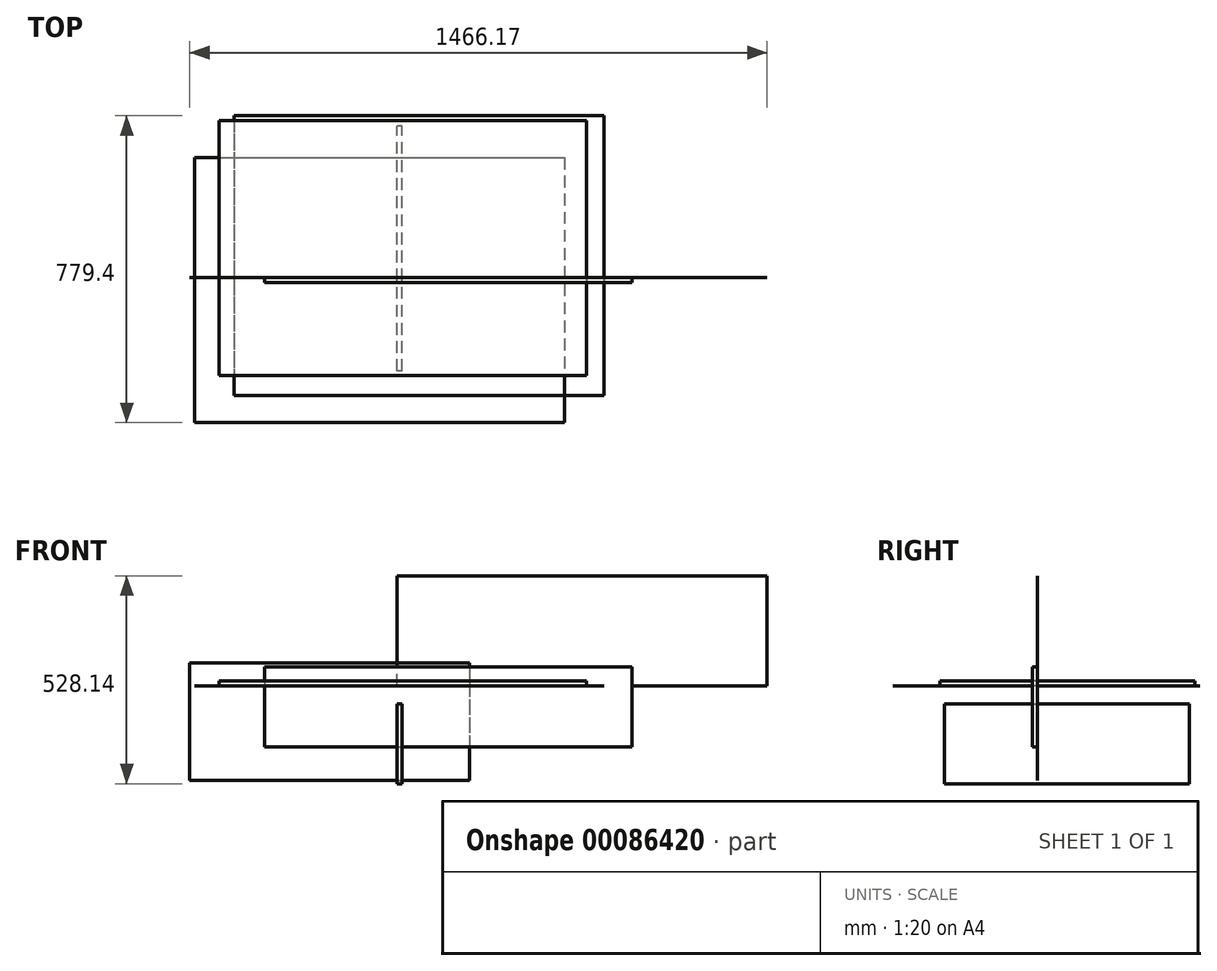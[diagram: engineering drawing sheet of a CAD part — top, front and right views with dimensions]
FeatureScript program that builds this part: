
annotation { "Feature Type Name" : "Feature", "Feature Type Description" : "" }
export const myFeature = defineFeature(function(context is Context, id is Id, definition is map)
    precondition{}
    {
        {
            var Q0;
            Q0=qCreatedBy(makeId("Front.planeOp"),FACE);
            var sketch = newSketch(context, id + "F0", { "sketchPlane" : qUnion([Q0])});
            skLineSegment(sketch, "E0.bottom", {"start": v(0, 0) * mm, "end": v(939.8, 0) * mm});
            skLineSegment(sketch, "E0.top", {"start": v(0, 279.4) * mm, "end": v(939.8, 279.4) * mm});
            skLineSegment(sketch, "E0.left", {"start": v(0, 0) * mm, "end": v(0, 279.4) * mm});
            skLineSegment(sketch, "E0.right", {"start": v(939.8, 0) * mm, "end": v(939.8, 279.4) * mm});
            skSolve(sketch);
        }
        {
            var Q0;
            Q0=makeQuery(id+"F0.imprint","IMPRINT",FACE,{"disambiguationData":[TD([[makeQuery(id+"F0.imprint","IMPRINT",EDGE,{"derivedFrom":sQuery(id+"F0.wireOp",EDGE,"E0.bottom")}),1.0]])]});
            extrude(context, id + "F1", {"entities" : qUnion([Q0]), "depth" : 3 / 101.6 * mm});
        }
        {
            var Q0;
            Q0=qCreatedBy(makeId("Top.planeOp"),FACE);
            var sketch = newSketch(context, id + "F2", { "sketchPlane" : qUnion([Q0])});
            skLineSegment(sketch, "E1.bottom", {"start": v(-413.3, 411.7) * mm, "end": v(526.5, 411.7) * mm});
            skLineSegment(sketch, "E1.top", {"start": v(-413.3, -299.5) * mm, "end": v(526.5, -299.5) * mm});
            skLineSegment(sketch, "E1.left", {"start": v(-413.3, 411.7) * mm, "end": v(-413.3, -299.5) * mm});
            skLineSegment(sketch, "E1.right", {"start": v(526.5, 411.7) * mm, "end": v(526.5, -299.5) * mm});
            skSolve(sketch);
        }
        {
            var Q0;
            Q0=makeQuery(id+"F2.imprint","IMPRINT",FACE,{"disambiguationData":[TD([[makeQuery(id+"F2.imprint","IMPRINT",EDGE,{"derivedFrom":sQuery(id+"F2.wireOp",EDGE,"E1.bottom")}),-1.0]])]});
            extrude(context, id + "F3", {"entities" : qUnion([Q0]), "depth" : 3 / 101.6 * mm});
        }
        {
            var Q0;
            Q0=qCreatedBy(makeId("Top.planeOp"),FACE);
            var sketch = newSketch(context, id + "F4", { "sketchPlane" : qUnion([Q0])});
            skLineSegment(sketch, "E2.bottom", {"start": v(-514.58, 305.4) * mm, "end": v(425.22, 305.4) * mm});
            skLineSegment(sketch, "E2.top", {"start": v(-514.58, -367.7) * mm, "end": v(425.22, -367.7) * mm});
            skLineSegment(sketch, "E2.left", {"start": v(-514.58, 305.4) * mm, "end": v(-514.58, -367.7) * mm});
            skLineSegment(sketch, "E2.right", {"start": v(425.22, 305.4) * mm, "end": v(425.22, -367.7) * mm});
            skSolve(sketch);
        }
        {
            var Q0;
            Q0=makeQuery(id+"F4.imprint","IMPRINT",FACE,{"disambiguationData":[TD([[makeQuery(id+"F4.imprint","IMPRINT",EDGE,{"derivedFrom":sQuery(id+"F4.wireOp",EDGE,"E2.bottom")}),-1.0]])]});
            extrude(context, id + "F5", {"entities" : qUnion([Q0]), "depth" : 1 / 50.8 * mm});
        }
        {
            var Q0;
            Q0=qCreatedBy(makeId("Front.planeOp"),FACE);
            var sketch = newSketch(context, id + "F6", { "sketchPlane" : qUnion([Q0])});
            skLineSegment(sketch, "E3.bottom", {"start": v(-526.37, 57.78) * mm, "end": v(184.83, 57.78) * mm});
            skLineSegment(sketch, "E3.top", {"start": v(-526.37, -240.67) * mm, "end": v(184.83, -240.67) * mm});
            skLineSegment(sketch, "E3.left", {"start": v(-526.37, 57.78) * mm, "end": v(-526.37, -240.67) * mm});
            skLineSegment(sketch, "E3.right", {"start": v(184.83, 57.78) * mm, "end": v(184.83, -240.67) * mm});
            skSolve(sketch);
        }
        {
            var Q0;
            Q0=makeQuery(id+"F6.imprint","IMPRINT",FACE,{"disambiguationData":[TD([[makeQuery(id+"F6.imprint","IMPRINT",EDGE,{"derivedFrom":sQuery(id+"F6.wireOp",EDGE,"E3.bottom")}),-1.0]])]});
            extrude(context, id + "F7", {"entities" : qUnion([Q0]), "depth" : 3 / 101.6 * mm});
        }
        {
            var Q0;
            Q0=qCreatedBy(makeId("Front.planeOp"),FACE);
            var sketch = newSketch(context, id + "F8", { "sketchPlane" : qUnion([Q0])});
            skLineSegment(sketch, "E4.bottom", {"start": v(-336.77, 48.14) * mm, "end": v(596.68, 48.14) * mm});
            skLineSegment(sketch, "E4.top", {"start": v(-336.77, -155.06) * mm, "end": v(596.68, -155.06) * mm});
            skLineSegment(sketch, "E4.left", {"start": v(-336.77, 48.14) * mm, "end": v(-336.77, -155.06) * mm});
            skLineSegment(sketch, "E4.right", {"start": v(596.68, 48.14) * mm, "end": v(596.68, -155.06) * mm});
            skSolve(sketch);
        }
        {
            var Q0;
            Q0=makeQuery(id+"F8.imprint","IMPRINT",FACE,{"disambiguationData":[TD([[makeQuery(id+"F8.imprint","IMPRINT",EDGE,{"derivedFrom":sQuery(id+"F8.wireOp",EDGE,"E4.bottom")}),-1.0]])]});
            extrude(context, id + "F9", {"entities" : qUnion([Q0]), "depth" : 12.7 * mm});
        }
        {
            var Q0;
            Q0=qCreatedBy(makeId("Right.planeOp"),FACE);
            var sketch = newSketch(context, id + "F10", { "sketchPlane" : qUnion([Q0])});
            skLineSegment(sketch, "E5.bottom", {"start": v(-237.14, -45.54) * mm, "end": v(385.16, -45.54) * mm});
            skLineSegment(sketch, "E5.top", {"start": v(-237.14, -248.74) * mm, "end": v(385.16, -248.74) * mm});
            skLineSegment(sketch, "E5.left", {"start": v(-237.14, -45.54) * mm, "end": v(-237.14, -248.74) * mm});
            skLineSegment(sketch, "E5.right", {"start": v(385.16, -45.54) * mm, "end": v(385.16, -248.74) * mm});
            skSolve(sketch);
        }
        {
            var Q0;
            Q0=makeQuery(id+"F10.imprint","IMPRINT",FACE,{"disambiguationData":[TD([[makeQuery(id+"F10.imprint","IMPRINT",EDGE,{"derivedFrom":sQuery(id+"F10.wireOp",EDGE,"E5.bottom")}),-1.0]])]});
            extrude(context, id + "F11", {"entities" : qUnion([Q0]), "depth" : 12.7 * mm});
        }
        {
            var Q0;
            Q0=qCreatedBy(makeId("Top.planeOp"),FACE);
            var sketch = newSketch(context, id + "F12", { "sketchPlane" : qUnion([Q0])});
            skLineSegment(sketch, "E6.bottom", {"start": v(-451.64, 399.18) * mm, "end": v(481.81, 399.18) * mm});
            skLineSegment(sketch, "E6.top", {"start": v(-451.64, -248.52) * mm, "end": v(481.81, -248.52) * mm});
            skLineSegment(sketch, "E6.left", {"start": v(-451.64, 399.18) * mm, "end": v(-451.64, -248.52) * mm});
            skLineSegment(sketch, "E6.right", {"start": v(481.81, 399.18) * mm, "end": v(481.81, -248.52) * mm});
            skSolve(sketch);
        }
        {
            var Q0;
            Q0=makeQuery(id+"F12.imprint","IMPRINT",FACE,{"disambiguationData":[TD([[makeQuery(id+"F12.imprint","IMPRINT",EDGE,{"derivedFrom":sQuery(id+"F12.wireOp",EDGE,"E6.bottom")}),-1.0]])]});
            extrude(context, id + "F13", {"entities" : qUnion([Q0]), "depth" : 12.7 * mm});
        }
    });
